# Revit family: FP-Revit19-DH9060HL1-DryerStacked-90002787A
name_source: partatom
category: Specialty Equipment
units: mm (PartAtom-declared; Revit-internal decimal feet)

## family parameters
Always vertical = Yes
Cut with Voids When Loaded = Yes
Part Type = Normal
Room Calculation Point = No
Round Connector Dimension = Use Diameter
Shared = No
Work Plane-Based = No

## types (2) — shared parameters
Cavity - Depth = 665 mm  [stored 2.18176 ft]
Cavity - Height = 1900 mm  [stored 6.2336 ft]
Cavity - Width = 624 mm  [stored 2.04724 ft]
Chassis - Depth = 576 mm  [stored 1.88976 ft]
Chassis - Height = 827 mm  [stored 2.71325 ft]
Chassis - Width = 600 mm  [stored 1.9685 ft]
Connector Description - Electrical = 220 – 240 V, 50 Hz, 10 A circuit
Connector Description - Sanitary = Drain to tub or standpipe, MAX 1000mm - MIN 600mm high
Connector Description - Water = Water connection supplied from washer
Description = Heat Pump Dryer
FFL_Offset = 1005 mm  [stored 3.29724 ft]
Manufacturer = Fisher & Paykel Appliances Ltd
Material - Body = Fisher & Paykel - Grey
Material - Buttons and Dials = Fisher & Paykel - Black
Material - Display Panel = Fisher & Paykel - Black
Material - Door = Fisher & Paykel - Grey, Charcoal
Material - Glass = Fisher & Paykel - Glass, Black
Material - Trim = Fisher & Paykel - Steel, Chrome Plated
Product - Depth = 655 mm  [stored 2.14895 ft]
Product - Height = 875 mm  [stored 2.87073 ft]
Product - Width = 600 mm  [stored 1.9685 ft]
Visibility - Clearance Required = Yes
zero-valued in all types: Default Elevation

## per-type parameters (varying)
| type | Material - Front | Visibility - Stacking Kit Grey | Visibility - Stacking Kit White |
| DH9060HL1 | Fisher & Paykel - White | No | Yes |
| DH9060HLG1 | Fisher & Paykel - Grey, Charcoal | Yes | No |

note: column(s) folded — value = type name in every type: Model

note: [stored X ft] marks values corroborated as IEEE doubles in the binary element streams (Revit-internal decimal feet)

## geometry (parser evidence)
native form markers: Sweep x4
no freeform markers — native parametric forms only
